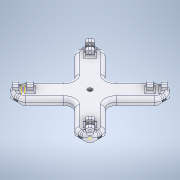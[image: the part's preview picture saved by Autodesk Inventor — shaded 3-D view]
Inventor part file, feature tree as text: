
AUTODESK INVENTOR PART (.ipt)
format: ipt  version: 2022 (Build 260153000, 153)  size: 635,904 bytes
history: native  units: in
note: dims shown in document units (in); Inventor stores cm internally (conversion verified against a paired STEP export)
features: sketch x6, plane x4, extrude x3, hole x3, fillet x3, pattern_circular x2, chamfer x1
ambient origin geometry x8: Origin, YZ Plane, XZ Plane, XY Plane, X Axis, Y Axis, Z Axis, Center Point
bodies: Solid1 (feature_tree)
feature tree (22):
  extrude  "Extrusion1"  Depth=2.9528in
  hole  "Hole2"  [1 undecoded]
  chamfer  "Chamfer1"  Distance=0.0394in Angle=45.0deg
  hole  "Hole5"  [1 undecoded]
  extrude  "Extrusion5"  Depth=0.2165in
  fillet  "Fillet3"  Radius=0.1575in
  hole  "Hole7"  [1 undecoded]
  pattern_circular  "Circular Pattern6"  [2 undecoded]
  extrude  "Extrusion14"  Depth=0.1575in
  fillet  "Fillet8"  Radius=0.1969in
  fillet  "Fillet9"  Radius=0.2165in
  sketch  "Sketch26"  dims[d90=1.4764in d97=0.2165in d98=0.1575in d99=0.9276in d100=0.1969in d101=0.0in d102=0.1575in d103=0.1969in d105=0.2165in d106=0.1082in d107=0.0591in d117=0.0787in d118=0.2362in d119=0.1575in d120=0.0787in d121=90.0deg d122=0.315in d123=0.8108in d124=0.1083in d125=0.0787in d129=1.5748in d130=360.0deg d199=135.0deg d200=90.0deg d201=0.5315in d202=0.5315in d203=1.1811in d205=180.0deg d207=0.0394in d208=0.0in d209=0.2756in d210=0.1181in d217=1.5748in d219=360.0deg d221=-0.5154in d222=1.5748in d223=360.0deg d131=0.0197in d132=0.0344in d155=0.0394in d156=0.0394in d157=0.0394in d158=0.0059in d159=0.0098in d160=0.0148in d161=0.5635in d162=0.0295in d163=0.8108in d164=0.0025in d165=0.0295in d166=0.0148in]
  plane  "Work Plane2"
  pattern_circular  "Circular Pattern7"  [2 undecoded]
  sketch  "Sketch1"  dims[d0=2.9528in d1=2.9528in]
  sketch  "Sketch4"  dims[d2=0.2165in d3=0.0in]
  sketch  "Sketch9"  dims[d15=0.1575in d16=0.2362in d17=1.0039in d18=0.0591in d19=90.0deg d20=0.315in d21=0.8108in d22=1.4764in]
  sketch  "Sketch13"  dims[d23=1.4764in d24=0.0394in d25=0.0787in d26=45.0deg]
  sketch  "Sketch24"  dims[d82=0.1575in d83=0.2362in d84=0.1575in d85=0.0787in d86=90.0deg d87=0.315in d88=0.8108in d89=1.1024in]
  plane  "Work Plane3"
  plane  "Work Plane4"
  plane  "Work Plane5"
note: 7 required parameter values undecoded (feature->parameter linkage not recoverable at this tier; creation-order binding heuristic only, values carry confidence <= 0.55)
